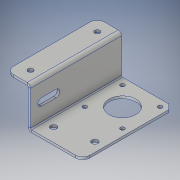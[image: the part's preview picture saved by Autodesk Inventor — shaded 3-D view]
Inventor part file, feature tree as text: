
AUTODESK INVENTOR PART (.ipt)
format: ipt  version: 2019 (Build 230136000, 136)  size: 256,000 bytes
history: native  units: mm
features: other x7, sketch x5, sheet_metal_op x3, chamfer x1
ambient origin geometry x8: Origin, YZ Plane, XZ Plane, XY Plane, X Axis, Y Axis, Z Axis, Center Point
bodies: Solid1 (feature_tree)
feature tree (16):
  sheet_metal_op  "Contour Flange1"
  other  "Corner Chamfer1"
  chamfer  "Corner Round2"
  sketch  "Sketch1"  dims[d0=20.0mm]
  other  "Plate1"
  sheet_metal_op  "Bend1"
  sheet_metal_op  "Corner1"
  sketch  "Sketch2"  dims[d1=32.0mm]
  sketch  "Sketch3"  dims[d2=43.0mm]
  sketch  "Sketch4"  dims[d3=2.0mm]
  sketch  "Sketch5"  dims[d4=0.2mm d5=0.2mm d6=0.2mm d7=0.8mm d8=75.0mm d9=0.8mm d10=2.0mm d11=8.0mm d12=0.2mm d13=0.8mm d14=22.2mm d15=31.0mm d16=3.4mm d17=2.0mm d18=0.0mm d19=4.0mm d20=6.0mm d21=45.0deg d22=4.2mm d25=2.0mm d26=0.0mm d28=10.0mm d30=10.0mm d31=5.65mm d32=5.0mm d33=7.5mm d34=17.5mm d35=11.0mm d36=35.0mm d37=2.0mm d38=0.0mm d41=6.0mm d45=2.0mm d46=0.0mm d47=15.0mm d48=12.0mm d49=6.0mm]
  other  "Cut1"
  other  "Cut2"
  other  "Cut3"
  other  "Cut4"
  other  "Definition1"
